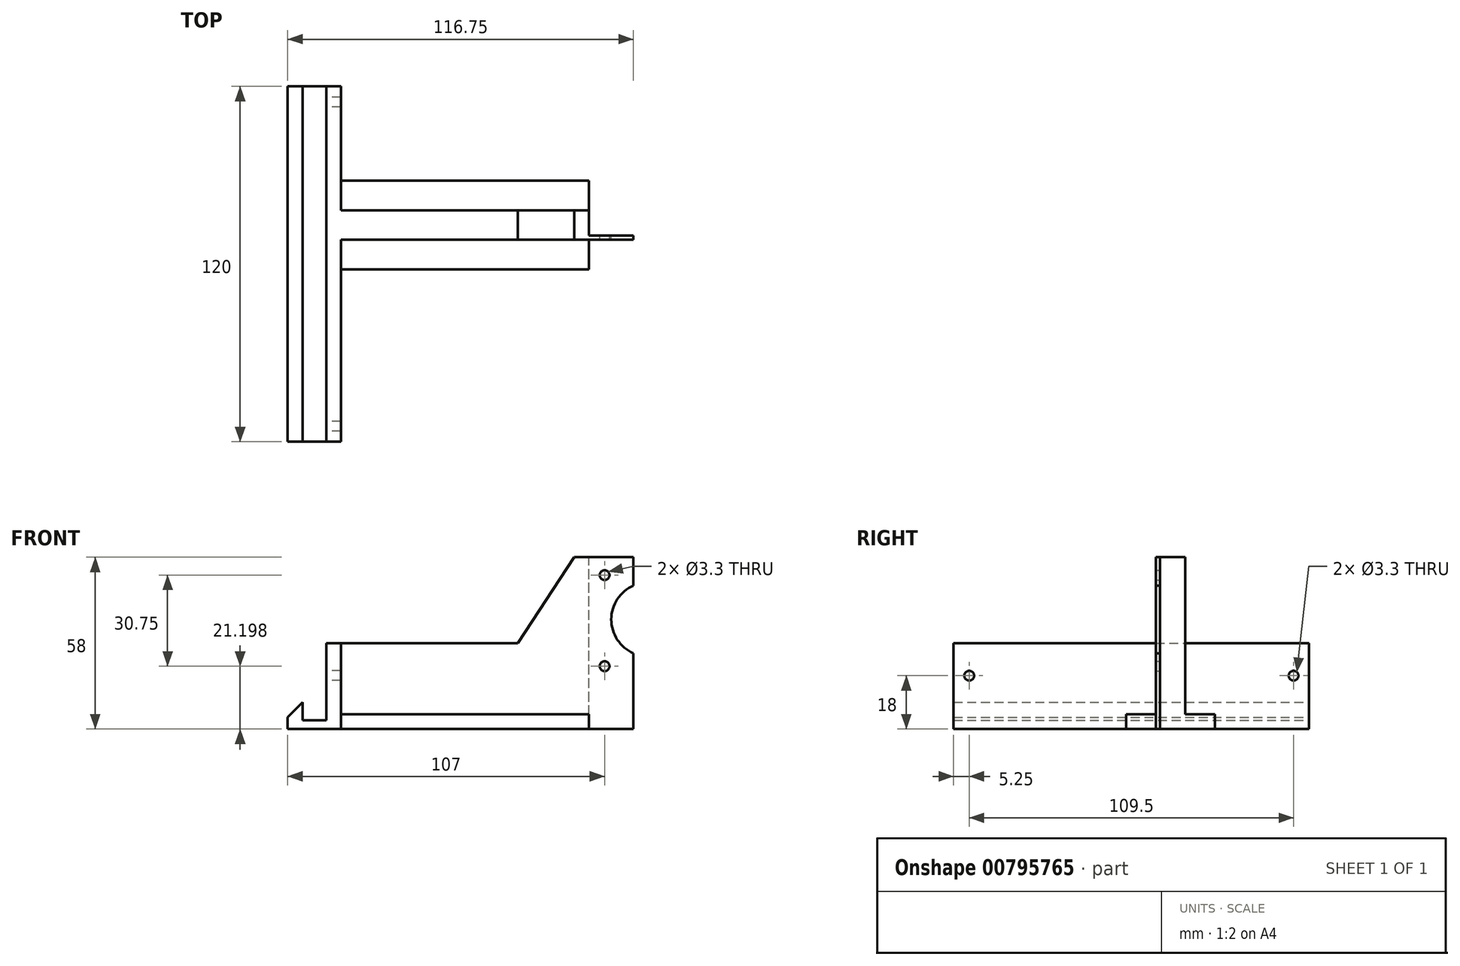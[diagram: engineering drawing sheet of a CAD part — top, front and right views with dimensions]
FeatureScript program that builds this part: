
annotation { "Feature Type Name" : "Feature", "Feature Type Description" : "" }
export const myFeature = defineFeature(function(context is Context, id is Id, definition is map)
    precondition{}
    {
        {
            var Q0;
            Q0=qCreatedBy(makeId("Front.planeOp"),FACE);
            cPlane(context, id + "F0", {"entities" : qUnion([Q0]), "cplaneType" : CPlaneType.OFFSET, "offset" : 9.7 * mm, "oppositeDirection" : true, "width" : 150 * mm, "height" : 150 * mm});
        }
        {
            var Q0;
            Q0=qCreatedBy(id+"F0.planeOp",FACE);
            var sketch = newSketch(context, id + "F1", { "sketchPlane" : qUnion([Q0])});
            skLineSegment(sketch, "E0", {"start": v(88.75, 0) * mm, "end": v(0, 0) * mm});
            skLineSegment(sketch, "E1", {"start": v(0, 0) * mm, "end": v(0, 29) * mm});
            skLineSegment(sketch, "E2", {"start": v(0, 29) * mm, "end": v(64.75, 29) * mm});
            skLineSegment(sketch, "E3", {"start": v(64.75, 29) * mm, "end": v(83.75, 58) * mm});
            skLineSegment(sketch, "E4", {"start": v(83.75, 58) * mm, "end": v(103.75, 58) * mm});
            skLineSegment(sketch, "E5", {"start": v(103.75, 58) * mm, "end": v(103.75, 48.46) * mm});
            skLineSegment(sketch, "E6", {"start": v(103.75, 0) * mm, "end": v(88.75, 0) * mm});
            skCircle(sketch, "E7", {"center": v(94, 21.2) * mm, "radius": 1.65 * mm});
            skCircle(sketch, "E8", {"center": v(94, 51.95) * mm, "radius": 1.65 * mm});
            skArc(sketch, "E9", {"start": v(103.75, 48.46) * mm, "mid": v(96.25, 37) * mm, "end": v(103.75, 25.54) * mm});
            skLineSegment(sketch, "E10.trimOffspring", {"start": v(103.75, 25.54) * mm, "end": v(103.75, 0) * mm});
            skLineSegment(sketch, "E11", {"start": v(88.75, 0) * mm, "end": v(88.75, 58) * mm});
            skSolve(sketch);
        }
        {
            var Q0;
            {var subQ0=sQuery(id+"F1.wireOp",EDGE,"E5");Q0=makeQuery(id+"F1.imprint","IMPRINT",FACE,{"disambiguationData":[TD([[makeQuery(id+"F1.imprint","IMPRINT",EDGE,{"derivedFrom":subQ0}),-1.0]])]});}
            extrude(context, id + "F2", {"entities" : qUnion([Q0]), "depth" : 1.5 * mm, "offsetDistance" : 25 * mm});
        }
        {
            var Q0;
            Q0=makeQuery(id+"F1.imprint","IMPRINT",FACE,{"disambiguationData":[TD([[makeQuery(id+"F1.imprint","IMPRINT",EDGE,{"derivedFrom":sQuery(id+"F1.wireOp",EDGE,"E0")}),-1.0]])]});
            extrude(context, id + "F3", {"entities" : qUnion([Q0]), "operationType" : NewBodyOperationType.ADD, "depth" : 1.5 * mm, "offsetDistance" : 25 * mm, "hasSecondDirection" : true, "secondDirectionOppositeDirection" : true, "secondDirectionDepth" : 8.5 * mm});
        }
        {
            var Q0;
            Q0=makeQuery(id+"F3.opExtrude","SWEPT_FACE",FACE,{"disambiguationData":[OSD([sQuery(id+"F1.wireOp",EDGE,"E1")])]});
            var sketch = newSketch(context, id + "F4", { "sketchPlane" : qUnion([Q0])});
            skLineSegment(sketch, "E12.bottom", {"start": v(-28.2, 5) * mm, "end": v(1.8, 5) * mm});
            skLineSegment(sketch, "E12.top", {"start": v(-28.2, 0) * mm, "end": v(1.8, 0) * mm});
            skLineSegment(sketch, "E12.left", {"start": v(-28.2, 5) * mm, "end": v(-28.2, 0) * mm});
            skLineSegment(sketch, "E12.right", {"start": v(1.8, 5) * mm, "end": v(1.8, 0) * mm});
            skSolve(sketch);
        }
        {
            var Q0;
            {var subQ0=sQuery(id+"F4.wireOp",EDGE,"E12.left");Q0=makeQuery(id+"F4.imprint","IMPRINT",FACE,{"disambiguationData":[TD([[makeQuery(id+"F4.imprint","IMPRINT",EDGE,{"derivedFrom":subQ0}),1.0]])]});}
            var Q1;
            {var subQ0=sQuery(id+"F4.wireOp",EDGE,"E12.right");Q1=makeQuery(id+"F4.imprint","IMPRINT",FACE,{"disambiguationData":[TD([[makeQuery(id+"F4.imprint","IMPRINT",EDGE,{"derivedFrom":subQ0}),-1.0]])]});}
            var Q2;
            Q2=makeQuery(id+"F3.opExtrude","SWEPT_FACE",FACE,{"disambiguationData":[OSD([sQuery(id+"F1.wireOp",EDGE,"E11")])]});
            extrude(context, id + "F5", {"entities" : qUnion([Q0, Q1]), "operationType" : NewBodyOperationType.ADD, "endBound" : BoundingType.UP_TO_SURFACE, "oppositeDirection" : true, "depth" : 25 * mm, "endBoundEntityFace" : qUnion([Q2]), "offsetDistance" : 25 * mm});
        }
        {
            var Q0;
            Q0=qCreatedBy(makeId("Front.planeOp"),FACE);
            var sketch = newSketch(context, id + "F6", { "sketchPlane" : qUnion([Q0])});
            skPoint(sketch, "E13.start.orphan", {"position": v(0, 0) * mm});
            skLineSegment(sketch, "E14", {"start": v(-13, 0) * mm, "end": v(-13, 4) * mm});
            skLineSegment(sketch, "E15", {"start": v(-13, 4) * mm, "end": v(-8, 9) * mm});
            skLineSegment(sketch, "E16", {"start": v(-8, 9) * mm, "end": v(-8, 3) * mm});
            skLineSegment(sketch, "E17", {"start": v(-8, 3) * mm, "end": v(0, 3) * mm});
            skLineSegment(sketch, "E18.0", {"start": v(0, 29) * mm, "end": v(5, 29) * mm});
            skLineSegment(sketch, "E19", {"start": v(0, 3) * mm, "end": v(0, 29) * mm});
            skLineSegment(sketch, "E20.0", {"start": v(5, 0) * mm, "end": v(-13, 0) * mm});
            skLineSegment(sketch, "E21", {"start": v(5, 0) * mm, "end": v(5, 29) * mm});
            skPoint(sketch, "E22.orphan", {"position": v(64.75, 29) * mm});
            skPoint(sketch, "E23.orphan", {"position": v(88.75, 0) * mm});
            skSolve(sketch);
        }
        {
            var Q0;
            Q0 = qSketchRegion(id + "F6", true);
            extrude(context, id + "F7", {"entities" : qUnion([Q0]), "operationType" : NewBodyOperationType.ADD, "endBound" : BoundingType.SYMMETRIC, "depth" : 120 * mm, "offsetDistance" : 25 * mm});
        }
        {
            var Q0;
            {var subQ0=sQuery(id+"F4.wireOp",EDGE,"E12.top");var subQ1=sQuery(id+"F4.wireOp",EDGE,"E12.bottom");var subQ2=sQuery(id+"F1.wireOp",EDGE,"E1");Q0=makeQuery(id+"F7.boolean.opBoolean","MERGE",FACE,{"derivedFrom":[makeQuery(id+"F5.boolean.opBoolean","MERGE",FACE,{"derivedFrom":[makeQuery(id+"F3.opExtrude","SWEPT_FACE",FACE,{"disambiguationData":[OSD([subQ2])]}),makeQuery(id+"F5.opExtrude","CAP_FACE",FACE,{"disambiguationData":[OSD([subQ2,subQ1,subQ0,sQuery(id+"F4.wireOp",EDGE,"E12.left")])],"isStart":true}),makeQuery(id+"F5.opExtrude","CAP_FACE",FACE,{"disambiguationData":[OSD([subQ2,subQ1,subQ0,sQuery(id+"F4.wireOp",EDGE,"E12.right")])],"isStart":true})]}),makeQuery(id+"F7.opExtrude","SWEPT_FACE",FACE,{"disambiguationData":[OSD([sQuery(id+"F6.wireOp",EDGE,"E19")])]})]});}
            var sketch = newSketch(context, id + "F8", { "sketchPlane" : qUnion([Q0])});
            skPoint(sketch, "E24", {"position": v(54.75, 18) * mm});
            skPoint(sketch, "E25.MirrorP", {"position": v(-54.75, 18) * mm});
            skLineSegment(sketch, "E26", {"start": v(20, 29) * mm, "end": v(20, 12) * mm});
            skLineSegment(sketch, "E27", {"start": v(20, 12) * mm, "end": v(-20, 12) * mm});
            skLineSegment(sketch, "E28", {"start": v(-20, 12) * mm, "end": v(-20, 29) * mm});
            skPoint(sketch, "E29", {"position": v(0, 12) * mm});
            skSolve(sketch);
        }
        {
            var Q0;
            Q0=sQuery(id+"F8.wireOp",VERTEX,"E24");
            var Q1;
            Q1=sQuery(id+"F8.wireOp",VERTEX,"E25.MirrorP");
            var Q2;
            Q2=makeQuery(id+"F2.opExtrude","SWEPT_BODY",BODY,{"disambiguationData":[OSD([sQuery(id+"F1.wireOp",EDGE,"E4"),sQuery(id+"F1.wireOp",EDGE,"E5"),sQuery(id+"F1.wireOp",EDGE,"E6"),sQuery(id+"F1.wireOp",EDGE,"E7"),sQuery(id+"F1.wireOp",EDGE,"E8"),sQuery(id+"F1.wireOp",EDGE,"E9"),sQuery(id+"F1.wireOp",EDGE,"E10.trimOffspring"),sQuery(id+"F1.wireOp",EDGE,"E11")])]});
            hole(context, id + "F9", {"style" : HoleStyle.SIMPLE, "endStyle" : HoleEndStyle.THROUGH, "holeDiameter" : 3.3 * mm, "majorDiameter" : 5 * mm, "isTappedThrough" : true, "tappedDepth" : 12 * mm, "tapClearance" : 3, "startFromSketch" : true, "locations" : qUnion([Q0, Q1]), "scope" : qUnion([Q2])});
        }
    });
